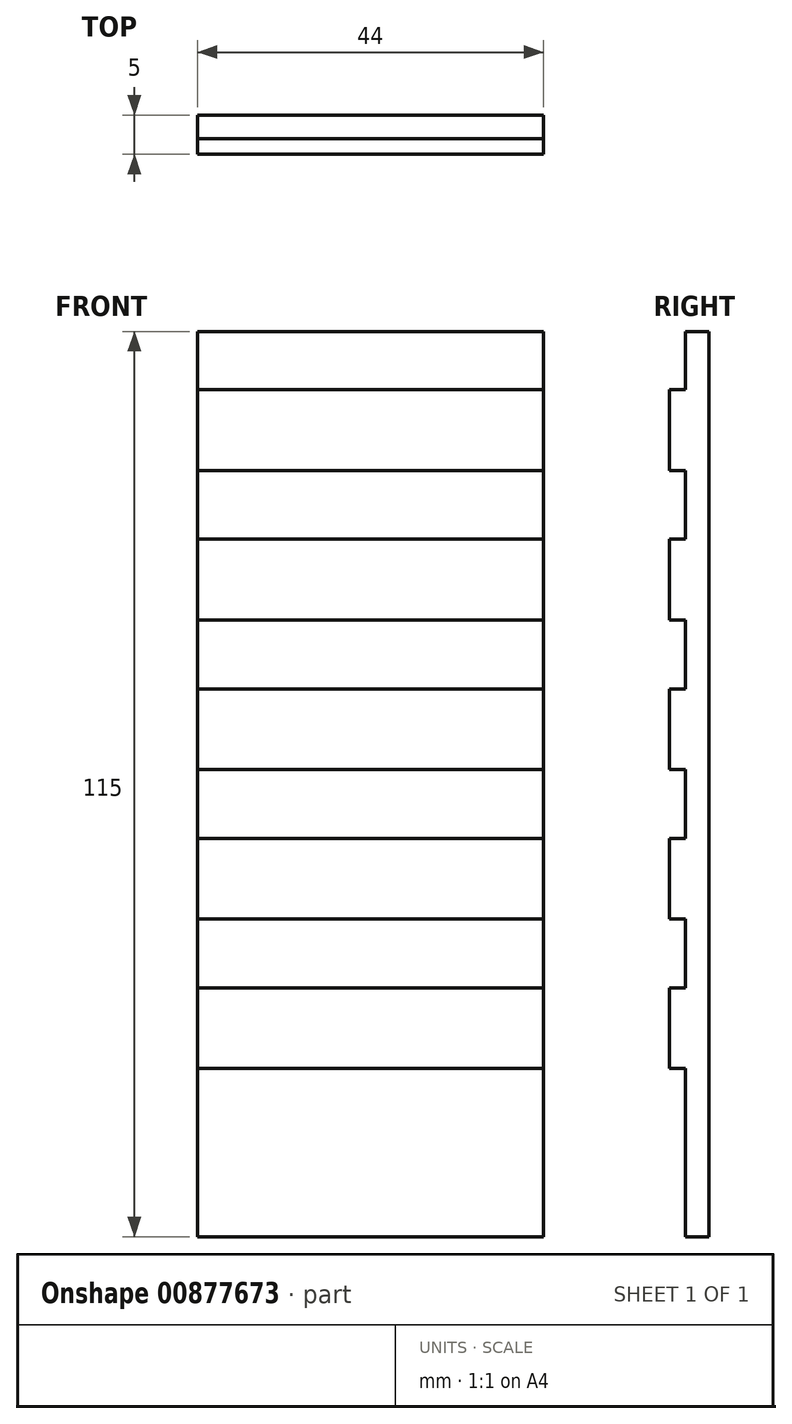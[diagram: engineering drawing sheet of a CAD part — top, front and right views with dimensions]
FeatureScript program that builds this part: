
annotation { "Feature Type Name" : "Feature", "Feature Type Description" : "" }
export const myFeature = defineFeature(function(context is Context, id is Id, definition is map)
    precondition{}
    {
        {
            var Q0;
            Q0=qCreatedBy(makeId("Front.planeOp"),FACE);
            var sketch = newSketch(context, id + "F0", { "sketchPlane" : qUnion([Q0])});
            skLineSegment(sketch, "E0.bottom", {"start": v(-22, 57.5) * mm, "end": v(22, 57.5) * mm});
            skLineSegment(sketch, "E0.top", {"start": v(-22, -57.5) * mm, "end": v(22, -57.5) * mm});
            skLineSegment(sketch, "E0.left", {"start": v(-22, 57.5) * mm, "end": v(-22, -57.5) * mm});
            skLineSegment(sketch, "E0.right", {"start": v(22, 57.5) * mm, "end": v(22, -57.5) * mm});
            skSolve(sketch);
        }
        {
            var Q0;
            Q0 = qSketchRegion(id + "F0", true);
            extrude(context, id + "F1", {"entities" : qUnion([Q0]), "depth" : 5 * mm, "offsetDistance" : 25 * mm});
        }
        {
            var Q0;
            Q0=makeQuery(id+"F1.opExtrude","CAP_FACE",FACE,{"disambiguationData":[OSD([sQuery(id+"F0.wireOp",EDGE,"E0.bottom"),sQuery(id+"F0.wireOp",EDGE,"E0.top"),sQuery(id+"F0.wireOp",EDGE,"E0.left"),sQuery(id+"F0.wireOp",EDGE,"E0.right")])],"isStart":false});
            var sketch = newSketch(context, id + "F2", { "sketchPlane" : qUnion([Q0])});
            skLineSegment(sketch, "E1", {"start": v(13.2, 57.5) * mm, "end": v(13.2, -57.5) * mm, "construction": true});
            skLineSegment(sketch, "E2", {"start": v(-13.2, 57.5) * mm, "end": v(-13.2, -57.5) * mm, "construction": true});
            skCircle(sketch, "E3", {"center": v(13.2, -12) * mm, "radius": 4.1 * mm});
            skCircle(sketch, "E4", {"center": v(13.2, -31) * mm, "radius": 4.1 * mm});
            skCircle(sketch, "E5", {"center": v(13.2, 7) * mm, "radius": 4.1 * mm});
            skCircle(sketch, "E6", {"center": v(13.2, 26) * mm, "radius": 4.1 * mm});
            skCircle(sketch, "E7", {"center": v(13.2, 45) * mm, "radius": 4.1 * mm});
            skCircle(sketch, "E8.MirrorC", {"center": v(-13.2, 7) * mm, "radius": 4.1 * mm});
            skCircle(sketch, "E9.MirrorC", {"center": v(-13.2, -12) * mm, "radius": 4.1 * mm});
            skCircle(sketch, "E10.MirrorC", {"center": v(-13.2, 45) * mm, "radius": 4.1 * mm});
            skCircle(sketch, "E11.MirrorC", {"center": v(-13.2, 26) * mm, "radius": 4.1 * mm});
            skCircle(sketch, "E12.MirrorC", {"center": v(-13.2, -31) * mm, "radius": 4.1 * mm});
            skSolve(sketch);
        }
        {
            var Q0;
            Q0=makeQuery(id+"F1.opExtrude","CAP_FACE",FACE,{"disambiguationData":[OSD([sQuery(id+"F0.wireOp",EDGE,"E0.bottom"),sQuery(id+"F0.wireOp",EDGE,"E0.top"),sQuery(id+"F0.wireOp",EDGE,"E0.left"),sQuery(id+"F0.wireOp",EDGE,"E0.right")])],"isStart":false});
            var sketch = newSketch(context, id + "F3", { "sketchPlane" : qUnion([Q0])});
            skCircle(sketch, "E13", {"center": v(13.75, -31) * mm, "radius": 2.08 * mm});
            skCircle(sketch, "E14", {"center": v(13.75, -12) * mm, "radius": 2.08 * mm});
            skCircle(sketch, "E15", {"center": v(13.75, 7) * mm, "radius": 2.08 * mm});
            skCircle(sketch, "E16", {"center": v(13.75, 26) * mm, "radius": 2.08 * mm});
            skCircle(sketch, "E17", {"center": v(13.75, 45) * mm, "radius": 2.08 * mm});
            skCircle(sketch, "E18.MirrorC", {"center": v(-13.75, 26) * mm, "radius": 2.08 * mm});
            skCircle(sketch, "E19.MirrorC", {"center": v(-13.75, 7) * mm, "radius": 2.08 * mm});
            skCircle(sketch, "E20.MirrorC", {"center": v(-13.75, 45) * mm, "radius": 2.08 * mm});
            skCircle(sketch, "E21.MirrorC", {"center": v(-13.75, -31) * mm, "radius": 2.08 * mm});
            skCircle(sketch, "E22.MirrorC", {"center": v(-13.75, -12) * mm, "radius": 2.08 * mm});
            skSolve(sketch);
        }
        {
            var Q0;
            Q0=makeQuery(id+"F1.opExtrude","CAP_FACE",FACE,{"disambiguationData":[OSD([sQuery(id+"F0.wireOp",EDGE,"E0.bottom"),sQuery(id+"F0.wireOp",EDGE,"E0.top"),sQuery(id+"F0.wireOp",EDGE,"E0.left"),sQuery(id+"F0.wireOp",EDGE,"E0.right")])],"isStart":true});
            var sketch = newSketch(context, id + "F4", { "sketchPlane" : qUnion([Q0])});
            skLineSegment(sketch, "E23.bottom", {"start": v(7, 17.5) * mm, "end": v(-7, 17.5) * mm});
            skLineSegment(sketch, "E23.top", {"start": v(7, 37.5) * mm, "end": v(-7, 37.5) * mm});
            skLineSegment(sketch, "E23.left", {"start": v(7, 17.5) * mm, "end": v(7, 37.5) * mm});
            skLineSegment(sketch, "E23.right", {"start": v(-7, 17.5) * mm, "end": v(-7, 37.5) * mm});
            skPoint(sketch, "E23.middle", {"position": v(0, 27.5) * mm});
            skLineSegment(sketch, "E24.MirrorCS", {"start": v(7, -17.5) * mm, "end": v(7, -37.5) * mm});
            skLineSegment(sketch, "E25.MirrorCS", {"start": v(7, -37.5) * mm, "end": v(-7, -37.5) * mm});
            skPoint(sketch, "E26.MirrorP", {"position": v(0, -27.5) * mm});
            skLineSegment(sketch, "E27.MirrorCS", {"start": v(7, -17.5) * mm, "end": v(-7, -17.5) * mm});
            skLineSegment(sketch, "E28.MirrorCS", {"start": v(-7, -17.5) * mm, "end": v(-7, -37.5) * mm});
            skSolve(sketch);
        }
        {
            var Q0;
            Q0=makeQuery(id+"F1.opExtrude","SWEPT_FACE",FACE,{"disambiguationData":[OSD([sQuery(id+"F0.wireOp",EDGE,"E0.right")])]});
            var sketch = newSketch(context, id + "F5", { "sketchPlane" : qUnion([Q0])});
            skLineSegment(sketch, "E29", {"start": v(-5, 50.1) * mm, "end": v(-5, 57.5) * mm});
            skLineSegment(sketch, "E30", {"start": v(-5, 57.5) * mm, "end": v(-3, 57.5) * mm});
            skLineSegment(sketch, "E31", {"start": v(-3, 57.5) * mm, "end": v(-3, 50.1) * mm});
            skLineSegment(sketch, "E32", {"start": v(-3, 50.1) * mm, "end": v(-5, 50.1) * mm});
            skSolve(sketch);
        }
        {
            var Q0;
            Q0 = qSketchRegion(id + "F5", true);
            extrude(context, id + "F6", {"entities" : qUnion([Q0]), "operationType" : NewBodyOperationType.REMOVE, "endBound" : BoundingType.THROUGH_ALL, "oppositeDirection" : true, "depth" : 25 * mm, "offsetDistance" : 25 * mm});
        }
        {
            var Q0;
            Q0=makeQuery(id+"F1.opExtrude","CAP_FACE",FACE,{"disambiguationData":[OSD([sQuery(id+"F0.wireOp",EDGE,"E0.bottom"),sQuery(id+"F0.wireOp",EDGE,"E0.top"),sQuery(id+"F0.wireOp",EDGE,"E0.left"),sQuery(id+"F0.wireOp",EDGE,"E0.right")])],"isStart":false});
            var sketch = newSketch(context, id + "F7", { "sketchPlane" : qUnion([Q0])});
            skLineSegment(sketch, "E33", {"start": v(-22, 39.85) * mm, "end": v(22, 39.85) * mm});
            skLineSegment(sketch, "E34", {"start": v(22, 39.85) * mm, "end": v(22, 31.1) * mm});
            skLineSegment(sketch, "E35", {"start": v(22, 31.1) * mm, "end": v(-22, 31.1) * mm});
            skLineSegment(sketch, "E36", {"start": v(-22, 31.1) * mm, "end": v(-22, 39.85) * mm});
            skLineSegment(sketch, "E37.bottom", {"start": v(22, 20.85) * mm, "end": v(-22, 20.85) * mm});
            skLineSegment(sketch, "E37.top", {"start": v(22, 12.1) * mm, "end": v(-22, 12.1) * mm});
            skLineSegment(sketch, "E37.left", {"start": v(22, 20.85) * mm, "end": v(22, 12.1) * mm});
            skLineSegment(sketch, "E37.right", {"start": v(-22, 20.85) * mm, "end": v(-22, 12.1) * mm});
            skPoint(sketch, "E37.middle", {"position": v(0, 16.47) * mm});
            skLineSegment(sketch, "E38.bottom", {"start": v(22, 1.85) * mm, "end": v(-22, 1.85) * mm});
            skLineSegment(sketch, "E38.top", {"start": v(22, -6.9) * mm, "end": v(-22, -6.9) * mm});
            skLineSegment(sketch, "E38.left", {"start": v(22, 1.85) * mm, "end": v(22, -6.9) * mm});
            skLineSegment(sketch, "E38.right", {"start": v(-22, 1.85) * mm, "end": v(-22, -6.9) * mm});
            skPoint(sketch, "E38.middle", {"position": v(0, -2.53) * mm});
            skLineSegment(sketch, "E39.bottom", {"start": v(22, -17.15) * mm, "end": v(-22, -17.15) * mm});
            skLineSegment(sketch, "E39.top", {"start": v(22, -25.9) * mm, "end": v(-22, -25.9) * mm});
            skLineSegment(sketch, "E39.left", {"start": v(22, -17.15) * mm, "end": v(22, -25.9) * mm});
            skLineSegment(sketch, "E39.right", {"start": v(-22, -17.15) * mm, "end": v(-22, -25.9) * mm});
            skPoint(sketch, "E39.middle", {"position": v(0, -21.53) * mm});
            skLineSegment(sketch, "E40.bottom", {"start": v(22, -57.5) * mm, "end": v(-22, -57.5) * mm});
            skLineSegment(sketch, "E40.top", {"start": v(22, -36.15) * mm, "end": v(-22, -36.15) * mm});
            skLineSegment(sketch, "E40.left", {"start": v(22, -57.5) * mm, "end": v(22, -36.15) * mm});
            skLineSegment(sketch, "E40.right", {"start": v(-22, -57.5) * mm, "end": v(-22, -36.15) * mm});
            skPoint(sketch, "E40.middle", {"position": v(0, -46.83) * mm});
            skSolve(sketch);
        }
        {
            var Q0;
            Q0 = qSketchRegion(id + "F7", true);
            extrude(context, id + "F8", {"entities" : qUnion([Q0]), "operationType" : NewBodyOperationType.REMOVE, "oppositeDirection" : true, "depth" : 2 * mm, "offsetDistance" : 25 * mm});
        }
    });
